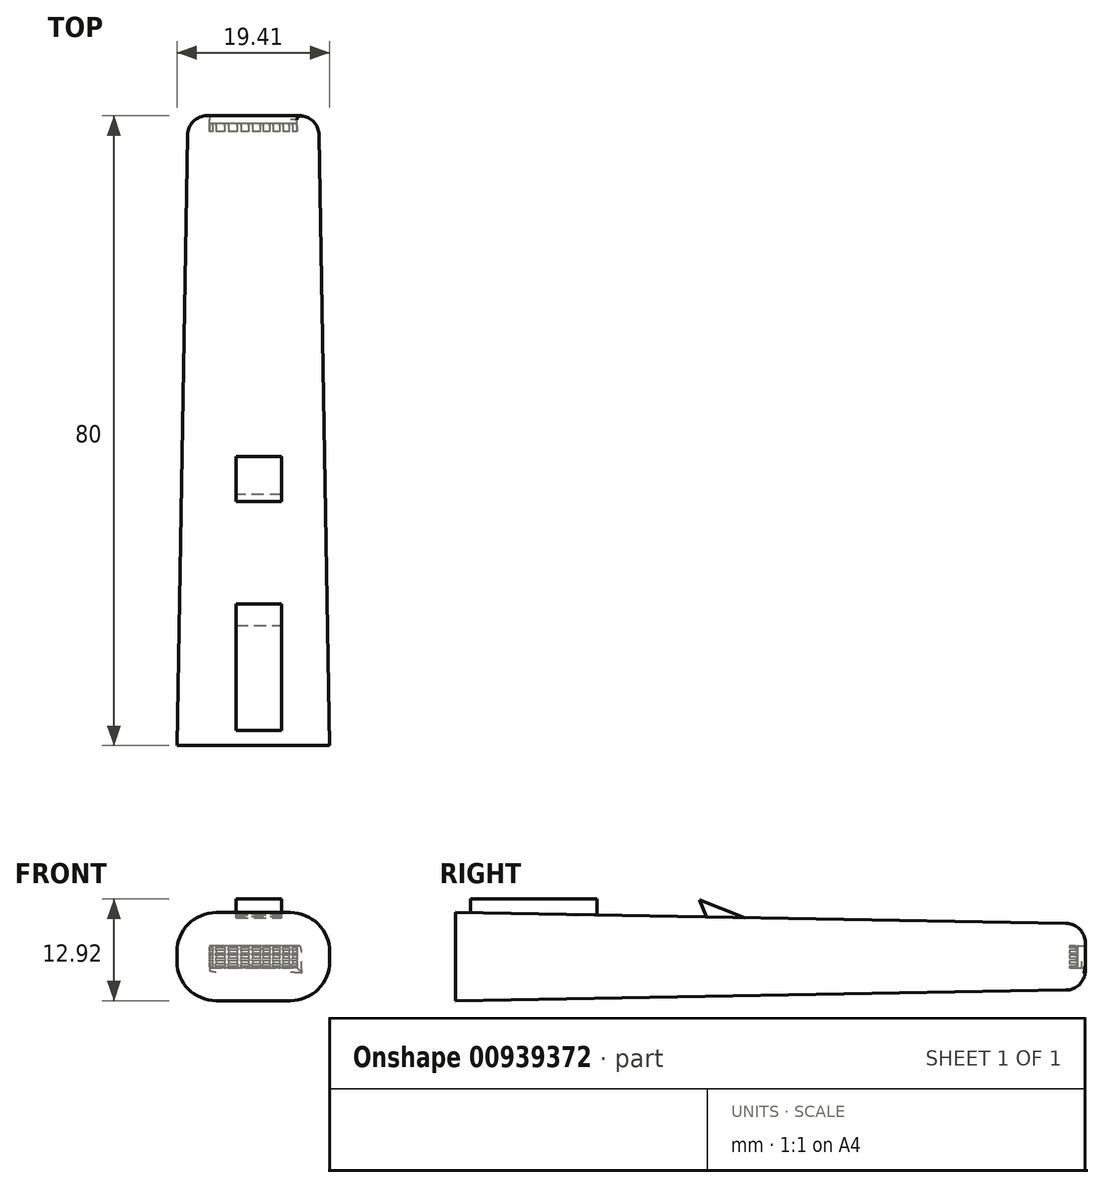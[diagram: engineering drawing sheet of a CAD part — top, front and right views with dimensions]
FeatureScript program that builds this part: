
annotation { "Feature Type Name" : "Feature", "Feature Type Description" : "" }
export const myFeature = defineFeature(function(context is Context, id is Id, definition is map)
    precondition{}
    {
        {
            var Q0;
            Q0=qCreatedBy(makeId("Front.planeOp"),FACE);
            var sketch = newSketch(context, id + "F0", { "sketchPlane" : qUnion([Q0])});
            skLineSegment(sketch, "E0.bottom", {"start": v(-5.42, 4.23) * mm, "end": v(4, 4.23) * mm});
            skLineSegment(sketch, "E0.top", {"start": v(-5.42, -6.96) * mm, "end": v(4, -6.96) * mm});
            skLineSegment(sketch, "E0.left", {"start": v(-10.42, -0.77) * mm, "end": v(-10.42, -1.96) * mm});
            skLineSegment(sketch, "E0.right", {"start": v(9, -0.77) * mm, "end": v(9, -1.96) * mm});
            skPoint(sketch, "E1.visualSharp", {"position": v(-10.42, 4.23) * mm});
            skArc(sketch, "E1.filletArc", {"start": v(-5.42, 4.23) * mm, "mid": v(-8.95, 2.76) * mm, "end": v(-10.42, -0.77) * mm});
            skPoint(sketch, "E2.visualSharp", {"position": v(9, 4.23) * mm});
            skArc(sketch, "E2.filletArc", {"start": v(9, -0.77) * mm, "mid": v(7.53, 2.76) * mm, "end": v(4, 4.23) * mm});
            skPoint(sketch, "E3.visualSharp", {"position": v(9, -6.96) * mm});
            skArc(sketch, "E3.filletArc", {"start": v(4, -6.96) * mm, "mid": v(7.53, -5.5) * mm, "end": v(9, -1.96) * mm});
            skPoint(sketch, "E4.visualSharp", {"position": v(-10.42, -6.96) * mm});
            skArc(sketch, "E4.filletArc", {"start": v(-10.42, -1.96) * mm, "mid": v(-8.95, -5.5) * mm, "end": v(-5.42, -6.96) * mm});
            skSolve(sketch);
        }
        {
            var Q0;
            Q0 = qSketchRegion(id + "F0", true);
            extrude(context, id + "F1", {"entities" : qUnion([Q0]), "oppositeDirection" : true, "depth" : 80 * mm, "offsetDistance" : 25 * mm, "hasDraft" : true, "draftAngle" : 1 * degree, "draftPullDirection" : true});
        }
        {
            var Q0;
            Q0=makeQuery(id+"F1.opExtrude","CAP_EDGE",EDGE,{"disambiguationData":[OSD([sQuery(id+"F0.wireOp",EDGE,"E0.bottom")])],"isStart":false});
            var Q1;
            Q1=makeQuery(id+"F1.opExtrude","CAP_EDGE",EDGE,{"disambiguationData":[OSD([sQuery(id+"F0.wireOp",EDGE,"E2.filletArc")])],"isStart":false});
            fillet(context, id + "F2", {"entities" : qUnion([Q0, Q1]), "radius" : 2.5 * mm, "tangentPropagation" : true, "allowEdgeOverflow" : false});
        }
        {
            var Q0;
            Q0=makeQuery(id+"F1.opExtrude","CAP_FACE",FACE,{"disambiguationData":[OSD([sQuery(id+"F0.wireOp",EDGE,"E0.bottom"),sQuery(id+"F0.wireOp",EDGE,"E0.top"),sQuery(id+"F0.wireOp",EDGE,"E0.left"),sQuery(id+"F0.wireOp",EDGE,"E0.right"),sQuery(id+"F0.wireOp",EDGE,"E1.filletArc"),sQuery(id+"F0.wireOp",EDGE,"E2.filletArc"),sQuery(id+"F0.wireOp",EDGE,"E3.filletArc"),sQuery(id+"F0.wireOp",EDGE,"E4.filletArc")])],"isStart":false});
            var sketch = newSketch(context, id + "F3", { "sketchPlane" : qUnion([Q0])});
            skLineSegment(sketch, "E5.bottom", {"start": v(-4.84, 0) * mm, "end": v(6.23, 0) * mm});
            skLineSegment(sketch, "E5.top", {"start": v(-4.84, -2.78) * mm, "end": v(6.23, -2.78) * mm});
            skLineSegment(sketch, "E5.left", {"start": v(-4.84, 0) * mm, "end": v(-4.84, -2.78) * mm});
            skLineSegment(sketch, "E5.right", {"start": v(6.23, 0) * mm, "end": v(6.23, -2.78) * mm});
            skSolve(sketch);
        }
        {
            var Q0;
            Q0 = qSketchRegion(id + "F3", true);
            extrude(context, id + "F4", {"entities" : qUnion([Q0]), "operationType" : NewBodyOperationType.REMOVE, "oppositeDirection" : true, "depth" : 2 * mm, "offsetDistance" : 25 * mm});
        }
        {
            var Q0;
            Q0=makeQuery(id+"F4.boolean.opBoolean","COPY",FACE,{"derivedFrom":makeQuery(id+"F4.opExtrude","CAP_FACE",FACE,{"disambiguationData":[OSD([sQuery(id+"F3.wireOp",EDGE,"E5.bottom"),sQuery(id+"F3.wireOp",EDGE,"E5.top"),sQuery(id+"F3.wireOp",EDGE,"E5.left"),sQuery(id+"F3.wireOp",EDGE,"E5.right")])],"isStart":false})});
            var sketch = newSketch(context, id + "F5", { "sketchPlane" : qUnion([Q0])});
            skLineSegment(sketch, "E6.bottom", {"start": v(-4.84, -0.28) * mm, "end": v(-4.27, -0.28) * mm});
            skLineSegment(sketch, "E6.top", {"start": v(-4.84, -0.56) * mm, "end": v(-4.27, -0.56) * mm});
            skLineSegment(sketch, "E6.left", {"start": v(-4.84, -0.28) * mm, "end": v(-4.84, -0.56) * mm});
            skLineSegment(sketch, "E6.right", {"start": v(6.23, -0.28) * mm, "end": v(6.23, -0.56) * mm});
            skLineSegment(sketch, "E7.bottom", {"start": v(-4.84, -0.95) * mm, "end": v(-4.27, -0.95) * mm});
            skLineSegment(sketch, "E7.top", {"start": v(-4.84, -1.23) * mm, "end": v(-4.27, -1.23) * mm});
            skLineSegment(sketch, "E7.left", {"start": v(-4.84, -0.95) * mm, "end": v(-4.84, -1.23) * mm});
            skLineSegment(sketch, "E7.right", {"start": v(6.23, -0.95) * mm, "end": v(6.23, -1.23) * mm});
            skLineSegment(sketch, "E8.bottom", {"start": v(-4.84, -1.57) * mm, "end": v(-4.27, -1.57) * mm});
            skLineSegment(sketch, "E8.top", {"start": v(-4.84, -1.9) * mm, "end": v(-4.27, -1.9) * mm});
            skLineSegment(sketch, "E8.left", {"start": v(-4.84, -1.57) * mm, "end": v(-4.84, -1.9) * mm});
            skLineSegment(sketch, "E8.right", {"start": v(6.23, -1.57) * mm, "end": v(6.23, -1.9) * mm});
            skLineSegment(sketch, "E9.bottom", {"start": v(-4.84, -2.29) * mm, "end": v(-4.27, -2.29) * mm});
            skLineSegment(sketch, "E9.top", {"start": v(-4.84, -2.6) * mm, "end": v(-4.27, -2.6) * mm});
            skLineSegment(sketch, "E9.left", {"start": v(-4.84, -2.29) * mm, "end": v(-4.84, -2.6) * mm});
            skLineSegment(sketch, "E9.right", {"start": v(6.23, -2.29) * mm, "end": v(6.23, -2.6) * mm});
            skLineSegment(sketch, "E10.bottom", {"start": v(-4.27, 0) * mm, "end": v(-3.86, 0) * mm});
            skLineSegment(sketch, "E10.top", {"start": v(-4.27, -2.78) * mm, "end": v(-3.86, -2.78) * mm});
            skLineSegment(sketch, "E10.left", {"start": v(-4.27, 0) * mm, "end": v(-4.27, -0.28) * mm});
            skLineSegment(sketch, "E10.right", {"start": v(-3.86, 0) * mm, "end": v(-3.86, -0.28) * mm});
            skLineSegment(sketch, "E11.bottom", {"start": v(-3.07, 0) * mm, "end": v(-2.62, 0) * mm});
            skLineSegment(sketch, "E11.top", {"start": v(-3.07, -2.78) * mm, "end": v(-2.62, -2.78) * mm});
            skLineSegment(sketch, "E11.left", {"start": v(-3.07, 0) * mm, "end": v(-3.07, -0.28) * mm});
            skLineSegment(sketch, "E11.right", {"start": v(-2.62, 0) * mm, "end": v(-2.62, -0.28) * mm});
            skLineSegment(sketch, "E12.bottom", {"start": v(-1.8, 0) * mm, "end": v(-1.35, 0) * mm});
            skLineSegment(sketch, "E12.top", {"start": v(-1.8, -2.78) * mm, "end": v(-1.35, -2.78) * mm});
            skLineSegment(sketch, "E12.left", {"start": v(-1.8, 0) * mm, "end": v(-1.8, -0.28) * mm});
            skLineSegment(sketch, "E12.right", {"start": v(-1.35, 0) * mm, "end": v(-1.35, -0.28) * mm});
            skLineSegment(sketch, "E13.bottom", {"start": v(-0.53, 0) * mm, "end": v(-0.12, 0) * mm});
            skLineSegment(sketch, "E13.top", {"start": v(-0.53, -2.78) * mm, "end": v(-0.12, -2.78) * mm});
            skLineSegment(sketch, "E13.left", {"start": v(-0.53, 0) * mm, "end": v(-0.53, -0.28) * mm});
            skLineSegment(sketch, "E13.right", {"start": v(-0.12, 0) * mm, "end": v(-0.12, -0.28) * mm});
            skLineSegment(sketch, "E14.bottom", {"start": v(0.83, 0) * mm, "end": v(1.29, 0) * mm});
            skLineSegment(sketch, "E14.top", {"start": v(0.83, -2.78) * mm, "end": v(1.29, -2.78) * mm});
            skLineSegment(sketch, "E14.left", {"start": v(0.83, 0) * mm, "end": v(0.83, -0.28) * mm});
            skLineSegment(sketch, "E14.right", {"start": v(1.29, 0) * mm, "end": v(1.29, -0.28) * mm});
            skLineSegment(sketch, "E15.bottom", {"start": v(2.25, 0) * mm, "end": v(2.74, 0) * mm});
            skLineSegment(sketch, "E15.top", {"start": v(2.25, -2.78) * mm, "end": v(2.74, -2.78) * mm});
            skLineSegment(sketch, "E15.left", {"start": v(2.25, 0) * mm, "end": v(2.25, -0.28) * mm});
            skLineSegment(sketch, "E15.right", {"start": v(2.74, 0) * mm, "end": v(2.74, -0.28) * mm});
            skLineSegment(sketch, "E16.bottom", {"start": v(3.85, 0) * mm, "end": v(4.34, 0) * mm});
            skLineSegment(sketch, "E16.top", {"start": v(3.85, -2.78) * mm, "end": v(4.34, -2.78) * mm});
            skLineSegment(sketch, "E16.left", {"start": v(3.85, 0) * mm, "end": v(3.85, -0.28) * mm});
            skLineSegment(sketch, "E16.right", {"start": v(4.34, 0) * mm, "end": v(4.34, -0.28) * mm});
            skLineSegment(sketch, "E17.bottom", {"start": v(5.44, 0) * mm, "end": v(5.9, 0) * mm});
            skLineSegment(sketch, "E17.top", {"start": v(5.44, -2.78) * mm, "end": v(5.9, -2.78) * mm});
            skLineSegment(sketch, "E17.left", {"start": v(5.44, 0) * mm, "end": v(5.44, -0.28) * mm});
            skLineSegment(sketch, "E17.right", {"start": v(5.9, 0) * mm, "end": v(5.9, -0.28) * mm});
            skLineSegment(sketch, "E18.trimOffspring", {"start": v(-3.86, -0.28) * mm, "end": v(-3.07, -0.28) * mm});
            skLineSegment(sketch, "E19.trimOffspring", {"start": v(-4.27, -0.56) * mm, "end": v(-4.27, -0.95) * mm});
            skLineSegment(sketch, "E20.trimOffspring", {"start": v(-3.86, -0.56) * mm, "end": v(-3.86, -0.95) * mm});
            skLineSegment(sketch, "E21.trimOffspring", {"start": v(-3.86, -0.56) * mm, "end": v(-3.07, -0.56) * mm});
            skLineSegment(sketch, "E22.trimOffspring", {"start": v(-3.86, -0.95) * mm, "end": v(-3.07, -0.95) * mm});
            skLineSegment(sketch, "E23.trimOffspring", {"start": v(-4.27, -1.23) * mm, "end": v(-4.27, -1.57) * mm});
            skLineSegment(sketch, "E24.trimOffspring", {"start": v(-3.86, -1.23) * mm, "end": v(-3.86, -1.57) * mm});
            skLineSegment(sketch, "E25.trimOffspring", {"start": v(-3.86, -1.23) * mm, "end": v(-3.07, -1.23) * mm});
            skLineSegment(sketch, "E26.trimOffspring", {"start": v(-3.86, -1.57) * mm, "end": v(-3.07, -1.57) * mm});
            skLineSegment(sketch, "E27.trimOffspring", {"start": v(-3.86, -1.9) * mm, "end": v(-3.07, -1.9) * mm});
            skLineSegment(sketch, "E28.trimOffspring", {"start": v(-3.86, -2.29) * mm, "end": v(-3.07, -2.29) * mm});
            skLineSegment(sketch, "E29.trimOffspring", {"start": v(-3.86, -2.6) * mm, "end": v(-3.07, -2.6) * mm});
            skLineSegment(sketch, "E30.trimOffspring", {"start": v(-4.27, -2.6) * mm, "end": v(-4.27, -2.78) * mm});
            skLineSegment(sketch, "E31.trimOffspring", {"start": v(-3.86, -2.6) * mm, "end": v(-3.86, -2.78) * mm});
            skLineSegment(sketch, "E32.trimOffspring", {"start": v(-4.27, -1.9) * mm, "end": v(-4.27, -2.29) * mm});
            skLineSegment(sketch, "E33.trimOffspring", {"start": v(-3.86, -1.9) * mm, "end": v(-3.86, -2.29) * mm});
            skLineSegment(sketch, "E34.trimOffspring", {"start": v(-3.07, -0.56) * mm, "end": v(-3.07, -0.95) * mm});
            skLineSegment(sketch, "E35.trimOffspring", {"start": v(-2.62, -0.56) * mm, "end": v(-2.62, -0.95) * mm});
            skLineSegment(sketch, "E36.trimOffspring", {"start": v(-3.07, -1.23) * mm, "end": v(-3.07, -1.57) * mm});
            skLineSegment(sketch, "E37.trimOffspring", {"start": v(-2.62, -1.23) * mm, "end": v(-2.62, -1.57) * mm});
            skLineSegment(sketch, "E38.trimOffspring", {"start": v(-3.07, -1.9) * mm, "end": v(-3.07, -2.29) * mm});
            skLineSegment(sketch, "E39.trimOffspring", {"start": v(-2.62, -1.9) * mm, "end": v(-2.62, -2.29) * mm});
            skLineSegment(sketch, "E40.trimOffspring", {"start": v(-3.07, -2.6) * mm, "end": v(-3.07, -2.78) * mm});
            skLineSegment(sketch, "E41.trimOffspring", {"start": v(-2.62, -2.6) * mm, "end": v(-2.62, -2.78) * mm});
            skLineSegment(sketch, "E42.trimOffspring", {"start": v(-2.62, -2.6) * mm, "end": v(-1.8, -2.6) * mm});
            skLineSegment(sketch, "E43.trimOffspring", {"start": v(-2.62, -2.29) * mm, "end": v(-1.8, -2.29) * mm});
            skLineSegment(sketch, "E44.trimOffspring", {"start": v(-2.62, -1.9) * mm, "end": v(-1.8, -1.9) * mm});
            skLineSegment(sketch, "E45.trimOffspring", {"start": v(-2.62, -1.57) * mm, "end": v(-1.8, -1.57) * mm});
            skLineSegment(sketch, "E46.trimOffspring", {"start": v(-2.62, -1.23) * mm, "end": v(-1.8, -1.23) * mm});
            skLineSegment(sketch, "E47.trimOffspring", {"start": v(-2.62, -0.95) * mm, "end": v(-1.8, -0.95) * mm});
            skLineSegment(sketch, "E48.trimOffspring", {"start": v(-2.62, -0.56) * mm, "end": v(-1.8, -0.56) * mm});
            skLineSegment(sketch, "E49.trimOffspring", {"start": v(-2.62, -0.28) * mm, "end": v(-1.8, -0.28) * mm});
            skLineSegment(sketch, "E50.trimOffspring", {"start": v(-1.35, -0.28) * mm, "end": v(-0.53, -0.28) * mm});
            skLineSegment(sketch, "E51.trimOffspring", {"start": v(-1.35, -0.56) * mm, "end": v(-0.53, -0.56) * mm});
            skLineSegment(sketch, "E52.trimOffspring", {"start": v(-1.35, -0.95) * mm, "end": v(-0.53, -0.95) * mm});
            skLineSegment(sketch, "E53.trimOffspring", {"start": v(-1.35, -1.23) * mm, "end": v(-0.53, -1.23) * mm});
            skLineSegment(sketch, "E54.trimOffspring", {"start": v(-1.35, -2.29) * mm, "end": v(-0.53, -2.29) * mm});
            skLineSegment(sketch, "E55.trimOffspring", {"start": v(-1.35, -2.6) * mm, "end": v(-0.53, -2.6) * mm});
            skLineSegment(sketch, "E56.trimOffspring", {"start": v(-1.35, -1.9) * mm, "end": v(-0.53, -1.9) * mm});
            skLineSegment(sketch, "E57.trimOffspring", {"start": v(-1.35, -1.57) * mm, "end": v(-0.53, -1.57) * mm});
            skLineSegment(sketch, "E58.trimOffspring", {"start": v(-1.8, -0.56) * mm, "end": v(-1.8, -1.57) * mm});
            skLineSegment(sketch, "E59.trimOffspring", {"start": v(-1.35, -0.56) * mm, "end": v(-1.35, -1.57) * mm});
            skLineSegment(sketch, "E60.trimOffspring", {"start": v(0.83, -0.56) * mm, "end": v(0.83, -0.95) * mm});
            skLineSegment(sketch, "E61.trimOffspring", {"start": v(1.29, -0.56) * mm, "end": v(1.29, -0.95) * mm});
            skLineSegment(sketch, "E62.trimOffspring", {"start": v(-0.53, -0.56) * mm, "end": v(-0.53, -0.95) * mm});
            skLineSegment(sketch, "E63.trimOffspring", {"start": v(-0.12, -0.56) * mm, "end": v(-0.12, -0.95) * mm});
            skLineSegment(sketch, "E64.trimOffspring", {"start": v(2.74, -0.56) * mm, "end": v(2.74, -0.95) * mm});
            skLineSegment(sketch, "E65.trimOffspring", {"start": v(2.25, -0.56) * mm, "end": v(2.25, -0.95) * mm});
            skLineSegment(sketch, "E66.trimOffspring", {"start": v(-0.12, -0.28) * mm, "end": v(0.83, -0.28) * mm});
            skLineSegment(sketch, "E67.trimOffspring", {"start": v(-0.12, -0.56) * mm, "end": v(0.83, -0.56) * mm});
            skLineSegment(sketch, "E68.trimOffspring", {"start": v(-0.12, -0.95) * mm, "end": v(0.83, -0.95) * mm});
            skLineSegment(sketch, "E69.trimOffspring", {"start": v(-0.12, -1.23) * mm, "end": v(0.83, -1.23) * mm});
            skLineSegment(sketch, "E70.trimOffspring", {"start": v(-0.12, -1.57) * mm, "end": v(0.83, -1.57) * mm});
            skLineSegment(sketch, "E71.trimOffspring", {"start": v(-0.12, -1.9) * mm, "end": v(0.83, -1.9) * mm});
            skLineSegment(sketch, "E72.trimOffspring", {"start": v(-0.12, -2.29) * mm, "end": v(0.83, -2.29) * mm});
            skLineSegment(sketch, "E73.trimOffspring", {"start": v(-1.8, -2.6) * mm, "end": v(-1.8, -2.78) * mm});
            skLineSegment(sketch, "E74.trimOffspring", {"start": v(-1.35, -2.6) * mm, "end": v(-1.35, -2.78) * mm});
            skLineSegment(sketch, "E75.trimOffspring", {"start": v(-0.53, -2.6) * mm, "end": v(-0.53, -2.78) * mm});
            skLineSegment(sketch, "E76.trimOffspring", {"start": v(-0.12, -2.6) * mm, "end": v(-0.12, -2.78) * mm});
            skLineSegment(sketch, "E77.trimOffspring", {"start": v(-1.8, -1.9) * mm, "end": v(-1.8, -2.29) * mm});
            skLineSegment(sketch, "E78.trimOffspring", {"start": v(-1.35, -1.9) * mm, "end": v(-1.35, -2.29) * mm});
            skLineSegment(sketch, "E79.trimOffspring", {"start": v(-0.12, -1.9) * mm, "end": v(-0.12, -2.29) * mm});
            skLineSegment(sketch, "E80.trimOffspring", {"start": v(-0.53, -1.9) * mm, "end": v(-0.53, -2.29) * mm});
            skLineSegment(sketch, "E81.trimOffspring", {"start": v(-0.53, -1.23) * mm, "end": v(-0.53, -1.57) * mm});
            skLineSegment(sketch, "E82.trimOffspring", {"start": v(-0.12, -1.23) * mm, "end": v(-0.12, -1.57) * mm});
            skLineSegment(sketch, "E83.trimOffspring", {"start": v(1.29, -0.95) * mm, "end": v(2.25, -0.95) * mm});
            skLineSegment(sketch, "E84.trimOffspring", {"start": v(1.29, -0.56) * mm, "end": v(2.25, -0.56) * mm});
            skLineSegment(sketch, "E85.trimOffspring", {"start": v(1.29, -0.28) * mm, "end": v(2.25, -0.28) * mm});
            skLineSegment(sketch, "E86.trimOffspring", {"start": v(0.83, -1.23) * mm, "end": v(0.83, -1.57) * mm});
            skLineSegment(sketch, "E87.trimOffspring", {"start": v(1.29, -1.23) * mm, "end": v(1.29, -1.57) * mm});
            skLineSegment(sketch, "E88.trimOffspring", {"start": v(1.29, -1.23) * mm, "end": v(2.25, -1.23) * mm});
            skLineSegment(sketch, "E89.trimOffspring", {"start": v(1.29, -1.57) * mm, "end": v(2.25, -1.57) * mm});
            skLineSegment(sketch, "E90.trimOffspring", {"start": v(0.83, -1.9) * mm, "end": v(0.83, -2.29) * mm});
            skLineSegment(sketch, "E91.trimOffspring", {"start": v(1.29, -1.9) * mm, "end": v(1.29, -2.29) * mm});
            skLineSegment(sketch, "E92.trimOffspring", {"start": v(1.29, -1.9) * mm, "end": v(2.25, -1.9) * mm});
            skLineSegment(sketch, "E93.trimOffspring", {"start": v(1.29, -2.29) * mm, "end": v(2.25, -2.29) * mm});
            skLineSegment(sketch, "E94.trimOffspring", {"start": v(0.83, -2.6) * mm, "end": v(0.83, -2.78) * mm});
            skLineSegment(sketch, "E95.trimOffspring", {"start": v(1.29, -2.6) * mm, "end": v(1.29, -2.78) * mm});
            skLineSegment(sketch, "E96.trimOffspring", {"start": v(1.29, -2.6) * mm, "end": v(2.25, -2.6) * mm});
            skLineSegment(sketch, "E97.trimOffspring", {"start": v(-0.12, -2.6) * mm, "end": v(0.83, -2.6) * mm});
            skLineSegment(sketch, "E98.trimOffspring", {"start": v(2.74, -0.28) * mm, "end": v(3.85, -0.28) * mm});
            skLineSegment(sketch, "E99.trimOffspring", {"start": v(2.74, -0.56) * mm, "end": v(3.85, -0.56) * mm});
            skLineSegment(sketch, "E100.trimOffspring", {"start": v(2.74, -0.95) * mm, "end": v(3.85, -0.95) * mm});
            skLineSegment(sketch, "E101.trimOffspring", {"start": v(2.74, -1.23) * mm, "end": v(3.85, -1.23) * mm});
            skLineSegment(sketch, "E102.trimOffspring", {"start": v(2.74, -1.57) * mm, "end": v(3.85, -1.57) * mm});
            skLineSegment(sketch, "E103.trimOffspring", {"start": v(2.74, -2.29) * mm, "end": v(3.85, -2.29) * mm});
            skLineSegment(sketch, "E104.trimOffspring", {"start": v(2.74, -1.9) * mm, "end": v(3.85, -1.9) * mm});
            skLineSegment(sketch, "E105.trimOffspring", {"start": v(2.74, -2.6) * mm, "end": v(3.85, -2.6) * mm});
            skLineSegment(sketch, "E106.trimOffspring", {"start": v(2.25, -2.6) * mm, "end": v(2.25, -2.78) * mm});
            skLineSegment(sketch, "E107.trimOffspring", {"start": v(2.25, -1.9) * mm, "end": v(2.25, -2.29) * mm});
            skLineSegment(sketch, "E108.trimOffspring", {"start": v(2.25, -1.23) * mm, "end": v(2.25, -1.57) * mm});
            skLineSegment(sketch, "E109.trimOffspring", {"start": v(2.74, -1.23) * mm, "end": v(2.74, -1.57) * mm});
            skLineSegment(sketch, "E110.trimOffspring", {"start": v(2.74, -1.9) * mm, "end": v(2.74, -2.29) * mm});
            skLineSegment(sketch, "E111.trimOffspring", {"start": v(2.74, -2.6) * mm, "end": v(2.74, -2.78) * mm});
            skLineSegment(sketch, "E112.trimOffspring", {"start": v(3.85, -0.56) * mm, "end": v(3.85, -0.95) * mm});
            skLineSegment(sketch, "E113.trimOffspring", {"start": v(4.34, -0.28) * mm, "end": v(5.44, -0.28) * mm});
            skLineSegment(sketch, "E114.trimOffspring", {"start": v(4.34, -0.56) * mm, "end": v(4.34, -0.95) * mm});
            skLineSegment(sketch, "E115.trimOffspring", {"start": v(4.34, -0.56) * mm, "end": v(5.44, -0.56) * mm});
            skLineSegment(sketch, "E116.trimOffspring", {"start": v(4.34, -0.95) * mm, "end": v(5.44, -0.95) * mm});
            skLineSegment(sketch, "E117.trimOffspring", {"start": v(4.34, -1.23) * mm, "end": v(5.44, -1.23) * mm});
            skLineSegment(sketch, "E118.trimOffspring", {"start": v(4.34, -1.57) * mm, "end": v(5.44, -1.57) * mm});
            skLineSegment(sketch, "E119.trimOffspring", {"start": v(4.34, -1.9) * mm, "end": v(5.44, -1.9) * mm});
            skLineSegment(sketch, "E120.trimOffspring", {"start": v(4.34, -2.29) * mm, "end": v(5.44, -2.29) * mm});
            skLineSegment(sketch, "E121.trimOffspring", {"start": v(4.34, -2.6) * mm, "end": v(5.44, -2.6) * mm});
            skLineSegment(sketch, "E122.trimOffspring", {"start": v(3.85, -2.6) * mm, "end": v(3.85, -2.78) * mm});
            skLineSegment(sketch, "E123.trimOffspring", {"start": v(3.85, -1.9) * mm, "end": v(3.85, -2.29) * mm});
            skLineSegment(sketch, "E124.trimOffspring", {"start": v(3.85, -1.23) * mm, "end": v(3.85, -1.57) * mm});
            skLineSegment(sketch, "E125.trimOffspring", {"start": v(4.34, -1.23) * mm, "end": v(4.34, -1.57) * mm});
            skLineSegment(sketch, "E126.trimOffspring", {"start": v(4.34, -1.9) * mm, "end": v(4.34, -2.29) * mm});
            skLineSegment(sketch, "E127.trimOffspring", {"start": v(4.34, -2.6) * mm, "end": v(4.34, -2.78) * mm});
            skLineSegment(sketch, "E128.trimOffspring", {"start": v(5.44, -2.6) * mm, "end": v(5.44, -2.78) * mm});
            skLineSegment(sketch, "E129.trimOffspring", {"start": v(5.44, -1.9) * mm, "end": v(5.44, -2.29) * mm});
            skLineSegment(sketch, "E130.trimOffspring", {"start": v(5.44, -1.23) * mm, "end": v(5.44, -1.57) * mm});
            skLineSegment(sketch, "E131.trimOffspring", {"start": v(5.44, -0.56) * mm, "end": v(5.44, -0.95) * mm});
            skLineSegment(sketch, "E132.trimOffspring", {"start": v(5.9, -0.28) * mm, "end": v(6.23, -0.28) * mm});
            skLineSegment(sketch, "E133.trimOffspring", {"start": v(5.9, -0.56) * mm, "end": v(6.23, -0.56) * mm});
            skLineSegment(sketch, "E134.trimOffspring", {"start": v(5.9, -0.95) * mm, "end": v(6.23, -0.95) * mm});
            skLineSegment(sketch, "E135.trimOffspring", {"start": v(5.9, -1.23) * mm, "end": v(6.23, -1.23) * mm});
            skLineSegment(sketch, "E136.trimOffspring", {"start": v(5.9, -1.57) * mm, "end": v(6.23, -1.57) * mm});
            skLineSegment(sketch, "E137.trimOffspring", {"start": v(5.9, -1.9) * mm, "end": v(6.23, -1.9) * mm});
            skLineSegment(sketch, "E138.trimOffspring", {"start": v(5.9, -2.29) * mm, "end": v(6.23, -2.29) * mm});
            skLineSegment(sketch, "E139.trimOffspring", {"start": v(5.9, -2.6) * mm, "end": v(6.23, -2.6) * mm});
            skLineSegment(sketch, "E140.trimOffspring", {"start": v(5.9, -2.6) * mm, "end": v(5.9, -2.78) * mm});
            skLineSegment(sketch, "E141.trimOffspring", {"start": v(5.9, -1.9) * mm, "end": v(5.9, -2.29) * mm});
            skLineSegment(sketch, "E142.trimOffspring", {"start": v(5.9, -1.23) * mm, "end": v(5.9, -1.57) * mm});
            skLineSegment(sketch, "E143.trimOffspring", {"start": v(5.9, -0.56) * mm, "end": v(5.9, -0.95) * mm});
            skSolve(sketch);
        }
        {
            var Q0;
            Q0 = qSketchRegion(id + "F5", true);
            extrude(context, id + "F6", {"entities" : qUnion([Q0]), "operationType" : NewBodyOperationType.ADD, "depth" : 1 * mm, "offsetDistance" : 25 * mm});
        }
        {
            var Q0;
            Q0=makeQuery(id+"F6.opExtrude","CAP_FACE",FACE,{"disambiguationData":[OSD([sQuery(id+"F5.wireOp",EDGE,"E6.bottom"),sQuery(id+"F5.wireOp",EDGE,"E6.top"),sQuery(id+"F5.wireOp",EDGE,"E6.left"),sQuery(id+"F5.wireOp",EDGE,"E6.right"),sQuery(id+"F5.wireOp",EDGE,"E7.bottom"),sQuery(id+"F5.wireOp",EDGE,"E7.top"),sQuery(id+"F5.wireOp",EDGE,"E7.left"),sQuery(id+"F5.wireOp",EDGE,"E7.right"),sQuery(id+"F5.wireOp",EDGE,"E8.bottom"),sQuery(id+"F5.wireOp",EDGE,"E8.top"),sQuery(id+"F5.wireOp",EDGE,"E8.left"),sQuery(id+"F5.wireOp",EDGE,"E8.right"),sQuery(id+"F5.wireOp",EDGE,"E9.bottom"),sQuery(id+"F5.wireOp",EDGE,"E9.top"),sQuery(id+"F5.wireOp",EDGE,"E9.left"),sQuery(id+"F5.wireOp",EDGE,"E9.right"),sQuery(id+"F5.wireOp",EDGE,"E10.bottom"),sQuery(id+"F5.wireOp",EDGE,"E10.top"),sQuery(id+"F5.wireOp",EDGE,"E10.left"),sQuery(id+"F5.wireOp",EDGE,"E10.right"),sQuery(id+"F5.wireOp",EDGE,"E11.bottom"),sQuery(id+"F5.wireOp",EDGE,"E11.top"),sQuery(id+"F5.wireOp",EDGE,"E11.left"),sQuery(id+"F5.wireOp",EDGE,"E11.right"),sQuery(id+"F5.wireOp",EDGE,"E12.bottom"),sQuery(id+"F5.wireOp",EDGE,"E12.top"),sQuery(id+"F5.wireOp",EDGE,"E12.left"),sQuery(id+"F5.wireOp",EDGE,"E12.right"),sQuery(id+"F5.wireOp",EDGE,"E13.bottom"),sQuery(id+"F5.wireOp",EDGE,"E13.top"),sQuery(id+"F5.wireOp",EDGE,"E13.left"),sQuery(id+"F5.wireOp",EDGE,"E13.right"),sQuery(id+"F5.wireOp",EDGE,"E14.bottom"),sQuery(id+"F5.wireOp",EDGE,"E14.top"),sQuery(id+"F5.wireOp",EDGE,"E14.left"),sQuery(id+"F5.wireOp",EDGE,"E14.right"),sQuery(id+"F5.wireOp",EDGE,"E15.bottom"),sQuery(id+"F5.wireOp",EDGE,"E15.top"),sQuery(id+"F5.wireOp",EDGE,"E15.left"),sQuery(id+"F5.wireOp",EDGE,"E15.right"),sQuery(id+"F5.wireOp",EDGE,"E16.bottom"),sQuery(id+"F5.wireOp",EDGE,"E16.top"),sQuery(id+"F5.wireOp",EDGE,"E16.left"),sQuery(id+"F5.wireOp",EDGE,"E16.right"),sQuery(id+"F5.wireOp",EDGE,"E17.bottom"),sQuery(id+"F5.wireOp",EDGE,"E17.top"),sQuery(id+"F5.wireOp",EDGE,"E17.left"),sQuery(id+"F5.wireOp",EDGE,"E17.right"),sQuery(id+"F5.wireOp",EDGE,"E18.trimOffspring"),sQuery(id+"F5.wireOp",EDGE,"E19.trimOffspring"),sQuery(id+"F5.wireOp",EDGE,"E20.trimOffspring"),sQuery(id+"F5.wireOp",EDGE,"E21.trimOffspring"),sQuery(id+"F5.wireOp",EDGE,"E22.trimOffspring"),sQuery(id+"F5.wireOp",EDGE,"E23.trimOffspring"),sQuery(id+"F5.wireOp",EDGE,"E24.trimOffspring"),sQuery(id+"F5.wireOp",EDGE,"E25.trimOffspring"),sQuery(id+"F5.wireOp",EDGE,"E26.trimOffspring"),sQuery(id+"F5.wireOp",EDGE,"E27.trimOffspring"),sQuery(id+"F5.wireOp",EDGE,"E28.trimOffspring"),sQuery(id+"F5.wireOp",EDGE,"E29.trimOffspring"),sQuery(id+"F5.wireOp",EDGE,"E30.trimOffspring"),sQuery(id+"F5.wireOp",EDGE,"E31.trimOffspring"),sQuery(id+"F5.wireOp",EDGE,"E32.trimOffspring"),sQuery(id+"F5.wireOp",EDGE,"E33.trimOffspring"),sQuery(id+"F5.wireOp",EDGE,"E34.trimOffspring"),sQuery(id+"F5.wireOp",EDGE,"E35.trimOffspring"),sQuery(id+"F5.wireOp",EDGE,"E36.trimOffspring"),sQuery(id+"F5.wireOp",EDGE,"E37.trimOffspring"),sQuery(id+"F5.wireOp",EDGE,"E38.trimOffspring"),sQuery(id+"F5.wireOp",EDGE,"E39.trimOffspring"),sQuery(id+"F5.wireOp",EDGE,"E40.trimOffspring"),sQuery(id+"F5.wireOp",EDGE,"E41.trimOffspring"),sQuery(id+"F5.wireOp",EDGE,"E42.trimOffspring"),sQuery(id+"F5.wireOp",EDGE,"E43.trimOffspring"),sQuery(id+"F5.wireOp",EDGE,"E44.trimOffspring"),sQuery(id+"F5.wireOp",EDGE,"E45.trimOffspring"),sQuery(id+"F5.wireOp",EDGE,"E46.trimOffspring"),sQuery(id+"F5.wireOp",EDGE,"E47.trimOffspring"),sQuery(id+"F5.wireOp",EDGE,"E48.trimOffspring"),sQuery(id+"F5.wireOp",EDGE,"E49.trimOffspring"),sQuery(id+"F5.wireOp",EDGE,"E50.trimOffspring"),sQuery(id+"F5.wireOp",EDGE,"E51.trimOffspring"),sQuery(id+"F5.wireOp",EDGE,"E52.trimOffspring"),sQuery(id+"F5.wireOp",EDGE,"E53.trimOffspring"),sQuery(id+"F5.wireOp",EDGE,"E54.trimOffspring"),sQuery(id+"F5.wireOp",EDGE,"E55.trimOffspring"),sQuery(id+"F5.wireOp",EDGE,"E56.trimOffspring"),sQuery(id+"F5.wireOp",EDGE,"E57.trimOffspring"),sQuery(id+"F5.wireOp",EDGE,"E58.trimOffspring"),sQuery(id+"F5.wireOp",EDGE,"E59.trimOffspring"),sQuery(id+"F5.wireOp",EDGE,"E60.trimOffspring"),sQuery(id+"F5.wireOp",EDGE,"E61.trimOffspring"),sQuery(id+"F5.wireOp",EDGE,"E62.trimOffspring"),sQuery(id+"F5.wireOp",EDGE,"E63.trimOffspring"),sQuery(id+"F5.wireOp",EDGE,"E64.trimOffspring"),sQuery(id+"F5.wireOp",EDGE,"E65.trimOffspring"),sQuery(id+"F5.wireOp",EDGE,"E66.trimOffspring"),sQuery(id+"F5.wireOp",EDGE,"E67.trimOffspring"),sQuery(id+"F5.wireOp",EDGE,"E68.trimOffspring"),sQuery(id+"F5.wireOp",EDGE,"E69.trimOffspring"),sQuery(id+"F5.wireOp",EDGE,"E70.trimOffspring"),sQuery(id+"F5.wireOp",EDGE,"E71.trimOffspring"),sQuery(id+"F5.wireOp",EDGE,"E72.trimOffspring"),sQuery(id+"F5.wireOp",EDGE,"E73.trimOffspring"),sQuery(id+"F5.wireOp",EDGE,"E74.trimOffspring"),sQuery(id+"F5.wireOp",EDGE,"E75.trimOffspring"),sQuery(id+"F5.wireOp",EDGE,"E76.trimOffspring"),sQuery(id+"F5.wireOp",EDGE,"E77.trimOffspring"),sQuery(id+"F5.wireOp",EDGE,"E78.trimOffspring"),sQuery(id+"F5.wireOp",EDGE,"E79.trimOffspring"),sQuery(id+"F5.wireOp",EDGE,"E80.trimOffspring"),sQuery(id+"F5.wireOp",EDGE,"E81.trimOffspring"),sQuery(id+"F5.wireOp",EDGE,"E82.trimOffspring"),sQuery(id+"F5.wireOp",EDGE,"E83.trimOffspring"),sQuery(id+"F5.wireOp",EDGE,"E84.trimOffspring"),sQuery(id+"F5.wireOp",EDGE,"E85.trimOffspring"),sQuery(id+"F5.wireOp",EDGE,"E86.trimOffspring"),sQuery(id+"F5.wireOp",EDGE,"E87.trimOffspring"),sQuery(id+"F5.wireOp",EDGE,"E88.trimOffspring"),sQuery(id+"F5.wireOp",EDGE,"E89.trimOffspring"),sQuery(id+"F5.wireOp",EDGE,"E90.trimOffspring"),sQuery(id+"F5.wireOp",EDGE,"E91.trimOffspring"),sQuery(id+"F5.wireOp",EDGE,"E92.trimOffspring"),sQuery(id+"F5.wireOp",EDGE,"E93.trimOffspring"),sQuery(id+"F5.wireOp",EDGE,"E94.trimOffspring"),sQuery(id+"F5.wireOp",EDGE,"E95.trimOffspring"),sQuery(id+"F5.wireOp",EDGE,"E96.trimOffspring"),sQuery(id+"F5.wireOp",EDGE,"E97.trimOffspring"),sQuery(id+"F5.wireOp",EDGE,"E98.trimOffspring"),sQuery(id+"F5.wireOp",EDGE,"E99.trimOffspring"),sQuery(id+"F5.wireOp",EDGE,"E100.trimOffspring"),sQuery(id+"F5.wireOp",EDGE,"E101.trimOffspring"),sQuery(id+"F5.wireOp",EDGE,"E102.trimOffspring"),sQuery(id+"F5.wireOp",EDGE,"E103.trimOffspring"),sQuery(id+"F5.wireOp",EDGE,"E104.trimOffspring"),sQuery(id+"F5.wireOp",EDGE,"E105.trimOffspring"),sQuery(id+"F5.wireOp",EDGE,"E106.trimOffspring"),sQuery(id+"F5.wireOp",EDGE,"E107.trimOffspring"),sQuery(id+"F5.wireOp",EDGE,"E108.trimOffspring"),sQuery(id+"F5.wireOp",EDGE,"E109.trimOffspring"),sQuery(id+"F5.wireOp",EDGE,"E110.trimOffspring"),sQuery(id+"F5.wireOp",EDGE,"E111.trimOffspring"),sQuery(id+"F5.wireOp",EDGE,"E112.trimOffspring"),sQuery(id+"F5.wireOp",EDGE,"E113.trimOffspring"),sQuery(id+"F5.wireOp",EDGE,"E114.trimOffspring"),sQuery(id+"F5.wireOp",EDGE,"E115.trimOffspring"),sQuery(id+"F5.wireOp",EDGE,"E116.trimOffspring"),sQuery(id+"F5.wireOp",EDGE,"E117.trimOffspring"),sQuery(id+"F5.wireOp",EDGE,"E118.trimOffspring"),sQuery(id+"F5.wireOp",EDGE,"E119.trimOffspring"),sQuery(id+"F5.wireOp",EDGE,"E120.trimOffspring"),sQuery(id+"F5.wireOp",EDGE,"E121.trimOffspring"),sQuery(id+"F5.wireOp",EDGE,"E122.trimOffspring"),sQuery(id+"F5.wireOp",EDGE,"E123.trimOffspring"),sQuery(id+"F5.wireOp",EDGE,"E124.trimOffspring"),sQuery(id+"F5.wireOp",EDGE,"E125.trimOffspring"),sQuery(id+"F5.wireOp",EDGE,"E126.trimOffspring"),sQuery(id+"F5.wireOp",EDGE,"E127.trimOffspring"),sQuery(id+"F5.wireOp",EDGE,"E128.trimOffspring"),sQuery(id+"F5.wireOp",EDGE,"E129.trimOffspring"),sQuery(id+"F5.wireOp",EDGE,"E130.trimOffspring"),sQuery(id+"F5.wireOp",EDGE,"E131.trimOffspring"),sQuery(id+"F5.wireOp",EDGE,"E132.trimOffspring"),sQuery(id+"F5.wireOp",EDGE,"E133.trimOffspring"),sQuery(id+"F5.wireOp",EDGE,"E134.trimOffspring"),sQuery(id+"F5.wireOp",EDGE,"E135.trimOffspring"),sQuery(id+"F5.wireOp",EDGE,"E136.trimOffspring"),sQuery(id+"F5.wireOp",EDGE,"E137.trimOffspring"),sQuery(id+"F5.wireOp",EDGE,"E138.trimOffspring"),sQuery(id+"F5.wireOp",EDGE,"E139.trimOffspring"),sQuery(id+"F5.wireOp",EDGE,"E140.trimOffspring"),sQuery(id+"F5.wireOp",EDGE,"E141.trimOffspring"),sQuery(id+"F5.wireOp",EDGE,"E142.trimOffspring"),sQuery(id+"F5.wireOp",EDGE,"E143.trimOffspring")])],"isStart":false});
            fillet(context, id + "F7", {"entities" : qUnion([Q0]), "radius" : 0.1 * mm, "tangentPropagation" : true, "allowEdgeOverflow" : false});
        }
        {
            var Q0;
            Q0=makeQuery(id+"F4.boolean.opBoolean","COPY",EDGE,{"derivedFrom":makeQuery(id+"F4.opExtrude","CAP_EDGE",EDGE,{"disambiguationData":[OSD([sQuery(id+"F3.wireOp",EDGE,"E5.bottom")])],"isStart":true})});
            var Q1;
            Q1=makeQuery(id+"F4.boolean.opBoolean","COPY",EDGE,{"derivedFrom":makeQuery(id+"F4.opExtrude","CAP_EDGE",EDGE,{"disambiguationData":[OSD([sQuery(id+"F3.wireOp",EDGE,"E5.left")])],"isStart":true})});
            var Q2;
            Q2=makeQuery(id+"F4.boolean.opBoolean","COPY",EDGE,{"derivedFrom":makeQuery(id+"F4.opExtrude","CAP_EDGE",EDGE,{"disambiguationData":[OSD([sQuery(id+"F3.wireOp",EDGE,"E5.top")])],"isStart":true})});
            var Q3;
            Q3=makeQuery(id+"F4.boolean.opBoolean","COPY",EDGE,{"derivedFrom":makeQuery(id+"F4.opExtrude","CAP_EDGE",EDGE,{"disambiguationData":[OSD([sQuery(id+"F3.wireOp",EDGE,"E5.right")])],"isStart":true})});
            fillet(context, id + "F8", {"entities" : qUnion([Q0, Q1, Q2, Q3]), "radius" : 0.5 * mm, "tangentPropagation" : true, "allowEdgeOverflow" : false});
        }
        {
            var Q0;
            Q0=qCreatedBy(makeId("Right.planeOp"),FACE);
            var sketch = newSketch(context, id + "F9", { "sketchPlane" : qUnion([Q0])});
            skLineSegment(sketch, "E144", {"start": v(36.86, 3.54) * mm, "end": v(30.98, 5.84) * mm});
            skLineSegment(sketch, "E145", {"start": v(30.98, 5.84) * mm, "end": v(31.9, 3.65) * mm});
            skLineSegment(sketch, "E146", {"start": v(31.9, 3.65) * mm, "end": v(36.86, 3.54) * mm});
            skLineSegment(sketch, "E147", {"start": v(17.95, 4) * mm, "end": v(17.95, 5.96) * mm});
            skLineSegment(sketch, "E148", {"start": v(17.95, 5.96) * mm, "end": v(1.91, 5.96) * mm});
            skLineSegment(sketch, "E149", {"start": v(1.91, 5.96) * mm, "end": v(1.91, 3.77) * mm});
            skLineSegment(sketch, "E150", {"start": v(1.91, 3.77) * mm, "end": v(17.95, 4) * mm});
            skSolve(sketch);
        }
        {
            var Q0;
            Q0 = qSketchRegion(id + "F9", true);
            extrude(context, id + "F10", {"entities" : qUnion([Q0]), "operationType" : NewBodyOperationType.ADD, "endBound" : BoundingType.SYMMETRIC, "depth" : 5.8 * mm, "offsetDistance" : 25 * mm});
        }
    });
